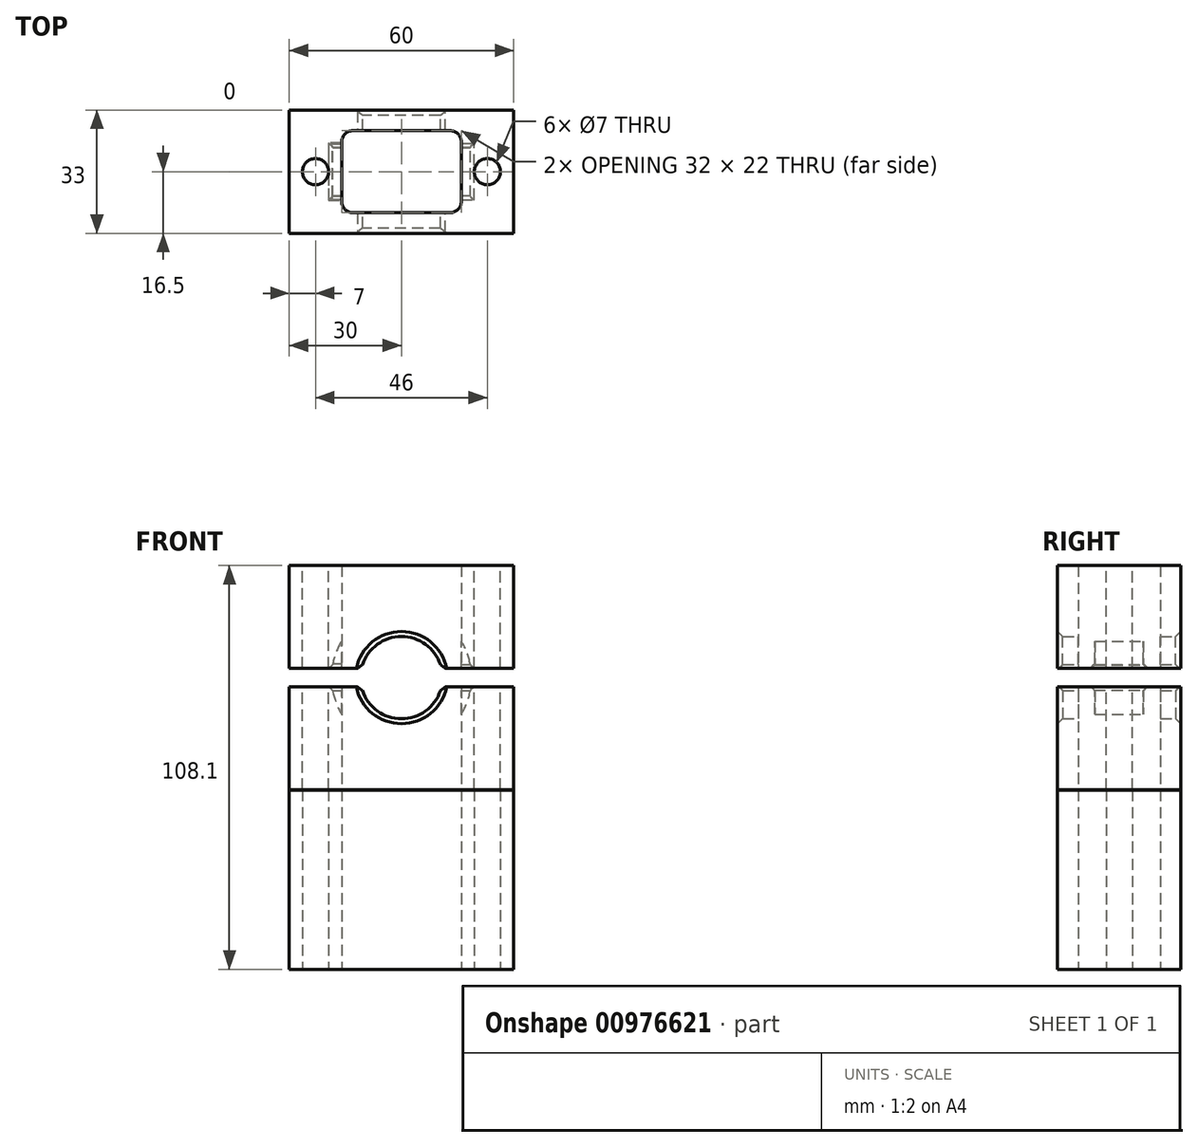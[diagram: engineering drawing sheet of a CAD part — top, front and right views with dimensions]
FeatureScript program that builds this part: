
annotation { "Feature Type Name" : "Feature", "Feature Type Description" : "" }
export const myFeature = defineFeature(function(context is Context, id is Id, definition is map)
    precondition{}
    {
        {
            var Q0;
            Q0=qCreatedBy(makeId("Front.planeOp"),FACE);
            var sketch = newSketch(context, id + "F0", { "sketchPlane" : qUnion([Q0])});
            skLineSegment(sketch, "E0.bottom", {"start": v(30, 30) * mm, "end": v(-30, 30) * mm});
            skLineSegment(sketch, "E0.top", {"start": v(30, -30) * mm, "end": v(-30, -30) * mm});
            skLineSegment(sketch, "E0.left", {"start": v(30, 30) * mm, "end": v(30, -30) * mm});
            skLineSegment(sketch, "E0.right", {"start": v(-30, 30) * mm, "end": v(-30, -30) * mm});
            skPoint(sketch, "E0.middle", {"position": v(0, 0) * mm});
            skCircle(sketch, "E1", {"center": v(0, 0) * mm, "radius": 11 * mm});
            skLineSegment(sketch, "E2", {"start": v(0, 0) * mm, "end": v(0, -54.5) * mm});
            skSolve(sketch);
        }
        {
            var Q0;
            Q0 = qSketchRegion(id + "F0", true);
            extrude(context, id + "F1", {"entities" : qUnion([Q0]), "depth" : 10 * mm, "offsetDistance" : 25 * mm});
        }
        {
            var Q0;
            Q0=makeQuery(id+"F1.opExtrude","CAP_FACE",FACE,{"disambiguationData":[OSD([sQuery(id+"F0.wireOp",EDGE,"E0.bottom"),sQuery(id+"F0.wireOp",EDGE,"E0.top"),sQuery(id+"F0.wireOp",EDGE,"E0.left"),sQuery(id+"F0.wireOp",EDGE,"E0.right"),sQuery(id+"F0.wireOp",EDGE,"E1")])],"isStart":false});
            var sketch = newSketch(context, id + "F2", { "sketchPlane" : qUnion([Q0])});
            skCircle(sketch, "E3", {"center": v(0, 0) * mm, "radius": 18.75 * mm});
            skLineSegment(sketch, "E4.bottom", {"start": v(30, 30) * mm, "end": v(-30, 30) * mm});
            skLineSegment(sketch, "E4.top", {"start": v(30, -30) * mm, "end": v(-30, -30) * mm});
            skLineSegment(sketch, "E4.left", {"start": v(30, 30) * mm, "end": v(30, -30) * mm});
            skLineSegment(sketch, "E4.right", {"start": v(-30, 30) * mm, "end": v(-30, -30) * mm});
            skSolve(sketch);
        }
        {
            var Q0;
            Q0 = qSketchRegion(id + "F2", true);
            extrude(context, id + "F3", {"entities" : qUnion([Q0]), "operationType" : NewBodyOperationType.ADD, "depth" : 13 * mm, "offsetDistance" : 25 * mm});
        }
        {
            var Q0;
            Q0=makeQuery(id+"F3.opExtrude","CAP_FACE",FACE,{"disambiguationData":[OSD([sQuery(id+"F2.wireOp",EDGE,"E3"),sQuery(id+"F2.wireOp",EDGE,"E4.bottom"),sQuery(id+"F2.wireOp",EDGE,"E4.top"),sQuery(id+"F2.wireOp",EDGE,"E4.left"),sQuery(id+"F2.wireOp",EDGE,"E4.right")])],"isStart":false});
            var sketch = newSketch(context, id + "F4", { "sketchPlane" : qUnion([Q0])});
            skCircle(sketch, "E5", {"center": v(0, 0) * mm, "radius": 11 * mm});
            skLineSegment(sketch, "E6.bottom", {"start": v(30, 30) * mm, "end": v(-30, 30) * mm});
            skLineSegment(sketch, "E6.top", {"start": v(30, -30) * mm, "end": v(-30, -30) * mm});
            skLineSegment(sketch, "E6.left", {"start": v(30, 30) * mm, "end": v(30, -30) * mm});
            skLineSegment(sketch, "E6.right", {"start": v(-30, 30) * mm, "end": v(-30, -30) * mm});
            skSolve(sketch);
        }
        {
            var Q0;
            Q0 = qSketchRegion(id + "F4", true);
            extrude(context, id + "F5", {"entities" : qUnion([Q0]), "operationType" : NewBodyOperationType.ADD, "depth" : 10 * mm, "offsetDistance" : 25 * mm});
        }
        {
            var Q0;
            Q0=makeQuery(id+"F5.boolean.opBoolean","MERGE",FACE,{"derivedFrom":[makeQuery(id+"F3.boolean.opBoolean","MERGE",FACE,{"derivedFrom":[makeQuery(id+"F1.opExtrude","SWEPT_FACE",FACE,{"disambiguationData":[OSD([sQuery(id+"F0.wireOp",EDGE,"E0.bottom")])]}),makeQuery(id+"F3.opExtrude","SWEPT_FACE",FACE,{"disambiguationData":[OSD([sQuery(id+"F2.wireOp",EDGE,"E4.bottom")])]})]}),makeQuery(id+"F5.opExtrude","SWEPT_FACE",FACE,{"disambiguationData":[OSD([sQuery(id+"F4.wireOp",EDGE,"E6.bottom")])]})]});
            var sketch = newSketch(context, id + "F6", { "sketchPlane" : qUnion([Q0])});
            skLineSegment(sketch, "E7", {"start": v(-30, -16.5) * mm, "end": v(-23, -16.5) * mm});
            skLineSegment(sketch, "E8", {"start": v(30, -16.5) * mm, "end": v(23, -16.5) * mm});
            skCircle(sketch, "E9", {"center": v(23, -16.5) * mm, "radius": 3.5 * mm});
            skCircle(sketch, "E10", {"center": v(-23, -16.5) * mm, "radius": 3.5 * mm});
            skSolve(sketch);
        }
        {
            var Q0;
            Q0=makeQuery(id+"F6.imprint","IMPRINT",FACE,{"disambiguationData":[TD([[makeQuery(id+"F6.imprint","IMPRINT",EDGE,{"derivedFrom":sQuery(id+"F6.wireOp",EDGE,"E10")}),1.0]])]});
            var Q1;
            Q1=makeQuery(id+"F6.imprint","IMPRINT",FACE,{"disambiguationData":[TD([[makeQuery(id+"F6.imprint","IMPRINT",EDGE,{"derivedFrom":sQuery(id+"F6.wireOp",EDGE,"E9")}),1.0]])]});
            extrude(context, id + "F7", {"entities" : qUnion([Q0, Q1]), "operationType" : NewBodyOperationType.REMOVE, "oppositeDirection" : true, "depth" : 60 * mm, "offsetDistance" : 25 * mm});
        }
        {
            var Q0;
            Q0=makeQuery(id+"F5.opExtrude","CAP_FACE",FACE,{"disambiguationData":[OSD([sQuery(id+"F4.wireOp",EDGE,"E5"),sQuery(id+"F4.wireOp",EDGE,"E6.bottom"),sQuery(id+"F4.wireOp",EDGE,"E6.top"),sQuery(id+"F4.wireOp",EDGE,"E6.left"),sQuery(id+"F4.wireOp",EDGE,"E6.right")])],"isStart":false});
            var sketch = newSketch(context, id + "F8", { "sketchPlane" : qUnion([Q0])});
            skLineSegment(sketch, "E11.bottom", {"start": v(35, 2.5) * mm, "end": v(-35, 2.5) * mm});
            skLineSegment(sketch, "E11.top", {"start": v(35, -2.5) * mm, "end": v(-35, -2.5) * mm});
            skLineSegment(sketch, "E11.left", {"start": v(35, 2.5) * mm, "end": v(35, -2.5) * mm});
            skLineSegment(sketch, "E11.right", {"start": v(-35, 2.5) * mm, "end": v(-35, -2.5) * mm});
            skPoint(sketch, "E11.middle", {"position": v(0, 0) * mm});
            skSolve(sketch);
        }
        {
            var Q0;
            Q0 = qSketchRegion(id + "F8", true);
            extrude(context, id + "F9", {"entities" : qUnion([Q0]), "operationType" : NewBodyOperationType.REMOVE, "endBound" : BoundingType.THROUGH_ALL, "oppositeDirection" : true, "depth" : 25 * mm, "offsetDistance" : 25 * mm});
        }
        {
            var Q0;
            {var subQ0=sQuery(id+"F0.wireOp",EDGE,"E1");Q0=makeQuery(id+"F9.boolean.opBoolean","SPLIT",FACE,{"disambiguationData":[TD([makeQuery(id+"F9.opExtrude","SWEPT_FACE",FACE,{"disambiguationData":[OSD([sQuery(id+"F8.wireOp",EDGE,"E11.top")])]})])],"derivedFrom":makeQuery(id+"F1.opExtrude","SWEPT_FACE",FACE,{"disambiguationData":[OSD([subQ0])]})});}
            var Q1;
            {var subQ4=sQuery(id+"F4.wireOp",EDGE,"E5");Q1=makeQuery(id+"F9.boolean.opBoolean","SPLIT",FACE,{"disambiguationData":[TD([makeQuery(id+"F9.opExtrude","SWEPT_FACE",FACE,{"disambiguationData":[OSD([sQuery(id+"F8.wireOp",EDGE,"E11.top")])]})])],"derivedFrom":makeQuery(id+"F5.opExtrude","SWEPT_FACE",FACE,{"disambiguationData":[OSD([subQ4])]})});}
            var Q2;
            Q2=makeQuery(id+"F9.boolean.opBoolean","INTERSECT",EDGE,{"disambiguationData":[OD(1.0)],"derivedFrom":[makeQuery(id+"F1.opExtrude","CAP_FACE",FACE,{"disambiguationData":[OSD([sQuery(id+"F0.wireOp",EDGE,"E0.bottom"),sQuery(id+"F0.wireOp",EDGE,"E0.top"),sQuery(id+"F0.wireOp",EDGE,"E0.left"),sQuery(id+"F0.wireOp",EDGE,"E0.right"),sQuery(id+"F0.wireOp",EDGE,"E1")])],"isStart":false}),makeQuery(id+"F9.opExtrude","SWEPT_FACE",FACE,{"disambiguationData":[OSD([sQuery(id+"F8.wireOp",EDGE,"E11.top")])]})]});
            var Q3;
            Q3=makeQuery(id+"F9.boolean.opBoolean","INTERSECT",EDGE,{"disambiguationData":[OD(1.0)],"derivedFrom":[makeQuery(id+"F5.opExtrude","CAP_FACE",FACE,{"disambiguationData":[OSD([sQuery(id+"F4.wireOp",EDGE,"E5"),sQuery(id+"F4.wireOp",EDGE,"E6.bottom"),sQuery(id+"F4.wireOp",EDGE,"E6.top"),sQuery(id+"F4.wireOp",EDGE,"E6.left"),sQuery(id+"F4.wireOp",EDGE,"E6.right")])],"isStart":true}),makeQuery(id+"F9.opExtrude","SWEPT_FACE",FACE,{"disambiguationData":[OSD([sQuery(id+"F8.wireOp",EDGE,"E11.top")])]})]});
            var Q4;
            Q4=makeQuery(id+"F9.boolean.opBoolean","INTERSECT",EDGE,{"disambiguationData":[OD(1.0)],"derivedFrom":[makeQuery(id+"F3.opExtrude","SWEPT_FACE",FACE,{"disambiguationData":[OSD([sQuery(id+"F2.wireOp",EDGE,"E3")])]}),makeQuery(id+"F9.opExtrude","SWEPT_FACE",FACE,{"disambiguationData":[OSD([sQuery(id+"F8.wireOp",EDGE,"E11.top")])]})]});
            var Q5;
            Q5=makeQuery(id+"F9.boolean.opBoolean","INTERSECT",EDGE,{"disambiguationData":[OD(0.0)],"derivedFrom":[makeQuery(id+"F1.opExtrude","CAP_FACE",FACE,{"disambiguationData":[OSD([sQuery(id+"F0.wireOp",EDGE,"E0.bottom"),sQuery(id+"F0.wireOp",EDGE,"E0.top"),sQuery(id+"F0.wireOp",EDGE,"E0.left"),sQuery(id+"F0.wireOp",EDGE,"E0.right"),sQuery(id+"F0.wireOp",EDGE,"E1")])],"isStart":false}),makeQuery(id+"F9.opExtrude","SWEPT_FACE",FACE,{"disambiguationData":[OSD([sQuery(id+"F8.wireOp",EDGE,"E11.top")])]})]});
            var Q6;
            Q6=makeQuery(id+"F9.boolean.opBoolean","INTERSECT",EDGE,{"disambiguationData":[OD(0.0)],"derivedFrom":[makeQuery(id+"F3.opExtrude","SWEPT_FACE",FACE,{"disambiguationData":[OSD([sQuery(id+"F2.wireOp",EDGE,"E3")])]}),makeQuery(id+"F9.opExtrude","SWEPT_FACE",FACE,{"disambiguationData":[OSD([sQuery(id+"F8.wireOp",EDGE,"E11.top")])]})]});
            var Q7;
            Q7=makeQuery(id+"F9.boolean.opBoolean","INTERSECT",EDGE,{"disambiguationData":[OD(0.0)],"derivedFrom":[makeQuery(id+"F5.opExtrude","CAP_FACE",FACE,{"disambiguationData":[OSD([sQuery(id+"F4.wireOp",EDGE,"E5"),sQuery(id+"F4.wireOp",EDGE,"E6.bottom"),sQuery(id+"F4.wireOp",EDGE,"E6.top"),sQuery(id+"F4.wireOp",EDGE,"E6.left"),sQuery(id+"F4.wireOp",EDGE,"E6.right")])],"isStart":true}),makeQuery(id+"F9.opExtrude","SWEPT_FACE",FACE,{"disambiguationData":[OSD([sQuery(id+"F8.wireOp",EDGE,"E11.top")])]})]});
            var Q8;
            Q8=makeQuery(id+"F9.boolean.opBoolean","INTERSECT",EDGE,{"disambiguationData":[OD(1.0)],"derivedFrom":[makeQuery(id+"F3.opExtrude","SWEPT_FACE",FACE,{"disambiguationData":[OSD([sQuery(id+"F2.wireOp",EDGE,"E3")])]}),makeQuery(id+"F9.opExtrude","SWEPT_FACE",FACE,{"disambiguationData":[OSD([sQuery(id+"F8.wireOp",EDGE,"E11.bottom")])]})]});
            var Q9;
            Q9=makeQuery(id+"F9.boolean.opBoolean","INTERSECT",EDGE,{"disambiguationData":[OD(1.0)],"derivedFrom":[makeQuery(id+"F5.opExtrude","CAP_FACE",FACE,{"disambiguationData":[OSD([sQuery(id+"F4.wireOp",EDGE,"E5"),sQuery(id+"F4.wireOp",EDGE,"E6.bottom"),sQuery(id+"F4.wireOp",EDGE,"E6.top"),sQuery(id+"F4.wireOp",EDGE,"E6.left"),sQuery(id+"F4.wireOp",EDGE,"E6.right")])],"isStart":true}),makeQuery(id+"F9.opExtrude","SWEPT_FACE",FACE,{"disambiguationData":[OSD([sQuery(id+"F8.wireOp",EDGE,"E11.bottom")])]})]});
            var Q10;
            Q10=makeQuery(id+"F9.boolean.opBoolean","INTERSECT",EDGE,{"disambiguationData":[OD(1.0)],"derivedFrom":[makeQuery(id+"F1.opExtrude","CAP_FACE",FACE,{"disambiguationData":[OSD([sQuery(id+"F0.wireOp",EDGE,"E0.bottom"),sQuery(id+"F0.wireOp",EDGE,"E0.top"),sQuery(id+"F0.wireOp",EDGE,"E0.left"),sQuery(id+"F0.wireOp",EDGE,"E0.right"),sQuery(id+"F0.wireOp",EDGE,"E1")])],"isStart":false}),makeQuery(id+"F9.opExtrude","SWEPT_FACE",FACE,{"disambiguationData":[OSD([sQuery(id+"F8.wireOp",EDGE,"E11.bottom")])]})]});
            var Q11;
            {var subQ4=sQuery(id+"F4.wireOp",EDGE,"E5");Q11=makeQuery(id+"F9.boolean.opBoolean","SPLIT",FACE,{"disambiguationData":[TD([makeQuery(id+"F9.opExtrude","SWEPT_FACE",FACE,{"disambiguationData":[OSD([sQuery(id+"F8.wireOp",EDGE,"E11.bottom")])]})])],"derivedFrom":makeQuery(id+"F5.opExtrude","SWEPT_FACE",FACE,{"disambiguationData":[OSD([subQ4])]})});}
            var Q12;
            {var subQ0=sQuery(id+"F0.wireOp",EDGE,"E1");Q12=makeQuery(id+"F9.boolean.opBoolean","SPLIT",FACE,{"disambiguationData":[TD([makeQuery(id+"F9.opExtrude","SWEPT_FACE",FACE,{"disambiguationData":[OSD([sQuery(id+"F8.wireOp",EDGE,"E11.bottom")])]})])],"derivedFrom":makeQuery(id+"F1.opExtrude","SWEPT_FACE",FACE,{"disambiguationData":[OSD([subQ0])]})});}
            var Q13;
            Q13=makeQuery(id+"F9.boolean.opBoolean","INTERSECT",EDGE,{"disambiguationData":[OD(0.0)],"derivedFrom":[makeQuery(id+"F1.opExtrude","CAP_FACE",FACE,{"disambiguationData":[OSD([sQuery(id+"F0.wireOp",EDGE,"E0.bottom"),sQuery(id+"F0.wireOp",EDGE,"E0.top"),sQuery(id+"F0.wireOp",EDGE,"E0.left"),sQuery(id+"F0.wireOp",EDGE,"E0.right"),sQuery(id+"F0.wireOp",EDGE,"E1")])],"isStart":false}),makeQuery(id+"F9.opExtrude","SWEPT_FACE",FACE,{"disambiguationData":[OSD([sQuery(id+"F8.wireOp",EDGE,"E11.bottom")])]})]});
            var Q14;
            Q14=makeQuery(id+"F9.boolean.opBoolean","INTERSECT",EDGE,{"disambiguationData":[OD(0.0)],"derivedFrom":[makeQuery(id+"F3.opExtrude","SWEPT_FACE",FACE,{"disambiguationData":[OSD([sQuery(id+"F2.wireOp",EDGE,"E3")])]}),makeQuery(id+"F9.opExtrude","SWEPT_FACE",FACE,{"disambiguationData":[OSD([sQuery(id+"F8.wireOp",EDGE,"E11.bottom")])]})]});
            var Q15;
            Q15=makeQuery(id+"F9.boolean.opBoolean","INTERSECT",EDGE,{"disambiguationData":[OD(0.0)],"derivedFrom":[makeQuery(id+"F5.opExtrude","CAP_FACE",FACE,{"disambiguationData":[OSD([sQuery(id+"F4.wireOp",EDGE,"E5"),sQuery(id+"F4.wireOp",EDGE,"E6.bottom"),sQuery(id+"F4.wireOp",EDGE,"E6.top"),sQuery(id+"F4.wireOp",EDGE,"E6.left"),sQuery(id+"F4.wireOp",EDGE,"E6.right")])],"isStart":true}),makeQuery(id+"F9.opExtrude","SWEPT_FACE",FACE,{"disambiguationData":[OSD([sQuery(id+"F8.wireOp",EDGE,"E11.bottom")])]})]});
            chamfer(context, id + "F10", {"entities" : qUnion([Q0, Q1, Q2, Q3, Q4, Q5, Q6, Q7, Q8, Q9, Q10, Q11, Q12, Q13, Q14, Q15]), "width" : 1 * mm, "tangentPropagation" : true});
        }
        {
            var Q0;
            Q0=qCreatedBy(makeId("Front.planeOp"),FACE);
            var sketch = newSketch(context, id + "F11", { "sketchPlane" : qUnion([Q0])});
            skLineSegment(sketch, "E12.bottom", {"start": v(30, -30.1) * mm, "end": v(-30, -30.1) * mm});
            skLineSegment(sketch, "E12.top", {"start": v(30, -78.1) * mm, "end": v(-30, -78.1) * mm});
            skLineSegment(sketch, "E12.left", {"start": v(30, -30.1) * mm, "end": v(30, -78.1) * mm});
            skLineSegment(sketch, "E12.right", {"start": v(-30, -30.1) * mm, "end": v(-30, -78.1) * mm});
            skPoint(sketch, "E12.middle", {"position": v(0, -54.1) * mm});
            skSolve(sketch);
        }
        {
            var Q0;
            Q0 = qSketchRegion(id + "F11", true);
            extrude(context, id + "F12", {"entities" : qUnion([Q0]), "depth" : 33 * mm, "offsetDistance" : 25 * mm});
        }
        {
            var Q0;
            Q0=makeQuery(id+"F12.opExtrude","SWEPT_FACE",FACE,{"disambiguationData":[OSD([sQuery(id+"F11.wireOp",EDGE,"E12.top")])]});
            var sketch = newSketch(context, id + "F13", { "sketchPlane" : qUnion([Q0])});
            skLineSegment(sketch, "E13", {"start": v(-30, 16.5) * mm, "end": v(-23, 16.5) * mm});
            skLineSegment(sketch, "E14", {"start": v(30, 16.5) * mm, "end": v(23, 16.5) * mm});
            skCircle(sketch, "E15", {"center": v(-23, 16.5) * mm, "radius": 3.5 * mm});
            skCircle(sketch, "E16", {"center": v(23, 16.5) * mm, "radius": 3.5 * mm});
            skLineSegment(sketch, "E17.bottom", {"start": v(16, 5.5) * mm, "end": v(-16, 5.5) * mm});
            skLineSegment(sketch, "E17.top", {"start": v(16, 27.5) * mm, "end": v(-16, 27.5) * mm});
            skLineSegment(sketch, "E17.left", {"start": v(16, 5.5) * mm, "end": v(16, 27.5) * mm});
            skLineSegment(sketch, "E17.right", {"start": v(-16, 5.5) * mm, "end": v(-16, 27.5) * mm});
            skPoint(sketch, "E17.middle", {"position": v(0, 16.5) * mm});
            skSolve(sketch);
        }
        {
            var Q0;
            Q0 = qSketchRegion(id + "F13", true);
            extrude(context, id + "F14", {"entities" : qUnion([Q0]), "operationType" : NewBodyOperationType.REMOVE, "endBound" : BoundingType.THROUGH_ALL, "oppositeDirection" : true, "depth" : 25 * mm, "offsetDistance" : 25 * mm});
        }
        {
            var Q0;
            Q0 = qSketchRegion(id + "F13", true);
            extrude(context, id + "F15", {"entities" : qUnion([Q0]), "operationType" : NewBodyOperationType.REMOVE, "endBound" : BoundingType.THROUGH_ALL, "oppositeDirection" : true, "depth" : 25 * mm, "offsetDistance" : 25 * mm});
        }
        {
            var Q0;
            Q0=makeQuery(id+"F14.boolean.opBoolean","COPY",EDGE,{"derivedFrom":makeQuery(id+"F14.opExtrude","SWEPT_EDGE",EDGE,{"disambiguationData":[OSD([sQuery(id+"F13.wireOp",EDGE,"E17.bottom"),sQuery(id+"F13.wireOp",EDGE,"E17.right")])]})});
            var Q1;
            Q1=makeQuery(id+"F14.boolean.opBoolean","COPY",EDGE,{"derivedFrom":makeQuery(id+"F14.opExtrude","SWEPT_EDGE",EDGE,{"disambiguationData":[OSD([sQuery(id+"F13.wireOp",EDGE,"E17.bottom"),sQuery(id+"F13.wireOp",EDGE,"E17.left")])]})});
            var Q2;
            Q2=makeQuery(id+"F14.boolean.opBoolean","COPY",EDGE,{"derivedFrom":makeQuery(id+"F14.opExtrude","SWEPT_EDGE",EDGE,{"disambiguationData":[OSD([sQuery(id+"F13.wireOp",EDGE,"E17.top"),sQuery(id+"F13.wireOp",EDGE,"E17.left")])]})});
            var Q3;
            Q3=makeQuery(id+"F14.boolean.opBoolean","COPY",EDGE,{"derivedFrom":makeQuery(id+"F14.opExtrude","SWEPT_EDGE",EDGE,{"disambiguationData":[OSD([sQuery(id+"F13.wireOp",EDGE,"E17.top"),sQuery(id+"F13.wireOp",EDGE,"E17.right")])]})});
            fillet(context, id + "F16", {"entities" : qUnion([Q0, Q1, Q2, Q3]), "radius" : 3 * mm, "tangentPropagation" : true, "allowEdgeOverflow" : false});
        }
    });
